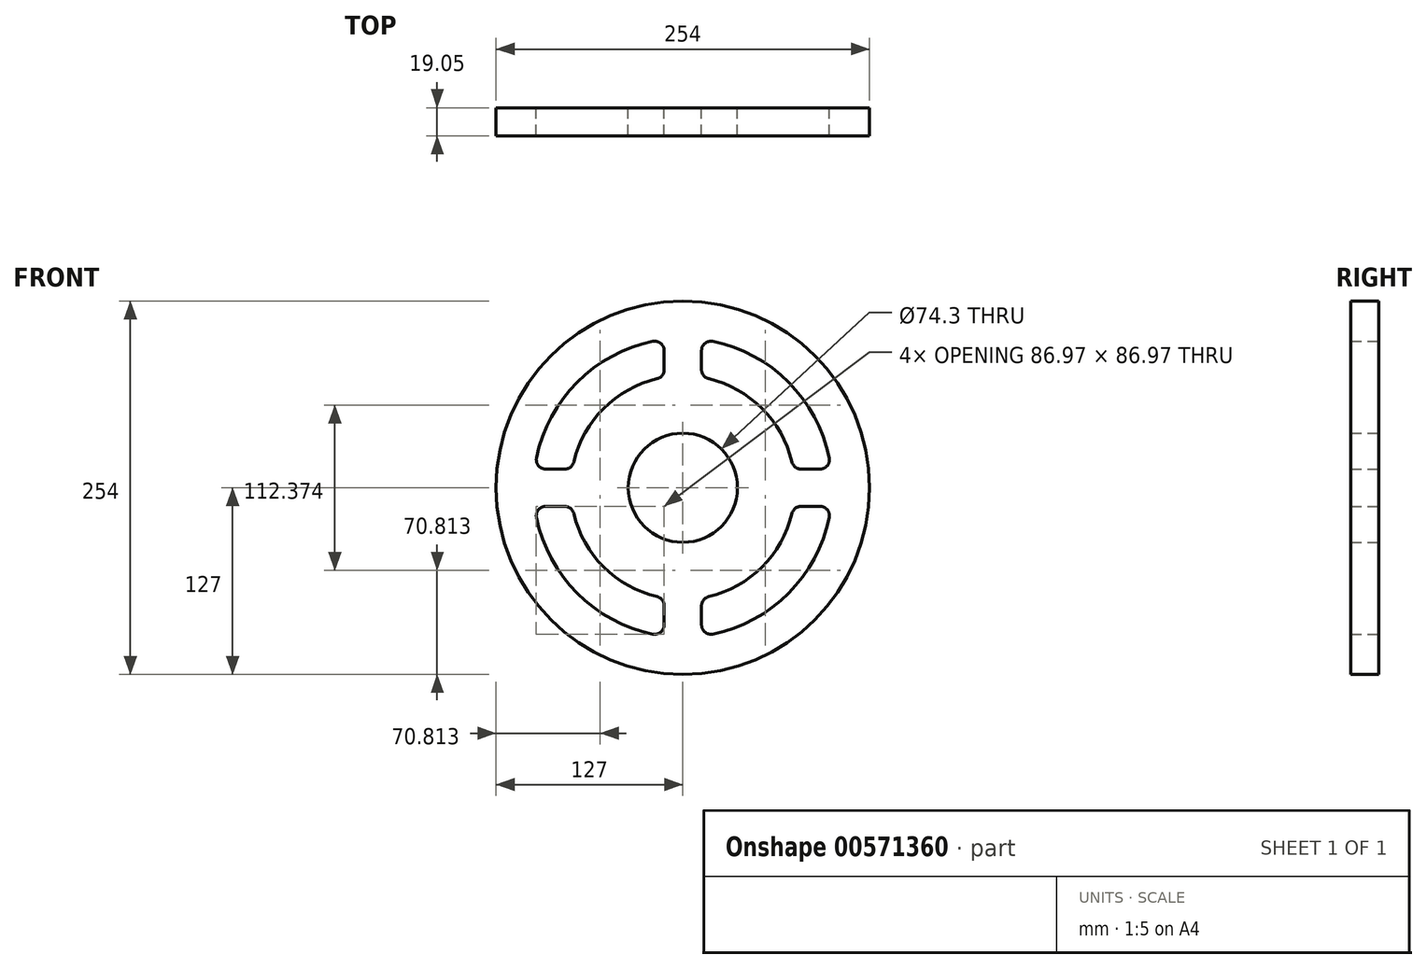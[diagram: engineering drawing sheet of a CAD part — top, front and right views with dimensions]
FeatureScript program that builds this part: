
annotation { "Feature Type Name" : "Feature", "Feature Type Description" : "" }
export const myFeature = defineFeature(function(context is Context, id is Id, definition is map)
    precondition{}
    {
        {
            var Q0;
            Q0=qCreatedBy(makeId("Front.planeOp"),FACE);
            var sketch = newSketch(context, id + "F0", { "sketchPlane" : qUnion([Q0])});
            skCircle(sketch, "E0", {"center": v(0, 0) * mm, "radius": 127 * mm});
            skCircle(sketch, "E1", {"center": v(0, 0) * mm, "radius": 32.39 * mm});
            skCircle(sketch, "E2", {"center": v(0, 0) * mm, "radius": 37.15 * mm});
            skSolve(sketch);
        }
        {
            var Q0;
            Q0=makeQuery(id+"F0.imprint","IMPRINT",FACE,{"disambiguationData":[TD([[makeQuery(id+"F0.imprint","IMPRINT",EDGE,{"derivedFrom":sQuery(id+"F0.wireOp",EDGE,"E0")}),1.0]])]});
            extrude(context, id + "F1", {"entities" : qUnion([Q0]), "depth" : 19.05 * mm, "offsetDistance" : 25.4 * mm});
        }
        {
            var Q0;
            Q0=makeQuery(id+"F1.opExtrude","CAP_FACE",FACE,{"disambiguationData":[OSD([sQuery(id+"F0.wireOp",EDGE,"E0"),sQuery(id+"F0.wireOp",EDGE,"E1")])],"isStart":true});
            var sketch = newSketch(context, id + "F2", { "sketchPlane" : qUnion([Q0])});
            skArc(sketch, "E3", {"start": v(74.14, 17.58) * mm, "mid": v(53.88, 53.88) * mm, "end": v(17.58, 74.14) * mm});
            skArc(sketch, "E4", {"start": v(99.55, 20.32) * mm, "mid": v(71.84, 71.84) * mm, "end": v(20.32, 99.55) * mm});
            skLineSegment(sketch, "E5.trimOffspring", {"start": v(-12.7, 80.32) * mm, "end": v(-12.7, 93.33) * mm});
            skLineSegment(sketch, "E6.trimOffspring", {"start": v(12.7, 80.32) * mm, "end": v(12.7, 93.33) * mm});
            skLineSegment(sketch, "E7.trimOffspring", {"start": v(80.32, 12.7) * mm, "end": v(93.33, 12.7) * mm});
            skLineSegment(sketch, "E8.trimOffspring", {"start": v(80.32, -12.7) * mm, "end": v(93.33, -12.7) * mm});
            skArc(sketch, "E9.trimOffspring", {"start": v(-17.58, 74.14) * mm, "mid": v(-53.88, 53.88) * mm, "end": v(-74.14, 17.58) * mm});
            skArc(sketch, "E10.trimOffspring", {"start": v(-20.32, 99.55) * mm, "mid": v(-71.84, 71.84) * mm, "end": v(-99.55, 20.32) * mm});
            skLineSegment(sketch, "E11.trimOffspring", {"start": v(-80.32, 12.7) * mm, "end": v(-93.33, 12.7) * mm});
            skLineSegment(sketch, "E12.trimOffspring", {"start": v(-80.32, -12.7) * mm, "end": v(-93.33, -12.7) * mm});
            skArc(sketch, "E13.trimOffspring", {"start": v(-74.14, -17.58) * mm, "mid": v(-53.88, -53.88) * mm, "end": v(-17.58, -74.14) * mm});
            skArc(sketch, "E14.trimOffspring", {"start": v(-99.55, -20.32) * mm, "mid": v(-71.84, -71.84) * mm, "end": v(-20.32, -99.55) * mm});
            skLineSegment(sketch, "E15.trimOffspring", {"start": v(-12.7, -80.32) * mm, "end": v(-12.7, -93.33) * mm});
            skLineSegment(sketch, "E16.trimOffspring", {"start": v(12.7, -80.32) * mm, "end": v(12.7, -93.33) * mm});
            skPoint(sketch, "E17.start.orphan", {"position": v(0, 12.7) * mm});
            skPoint(sketch, "E18.start.orphan", {"position": v(12.7, 0) * mm});
            skPoint(sketch, "E19.end.orphan", {"position": v(-12.7, 0) * mm});
            skPoint(sketch, "E20.start.orphan", {"position": v(0, -12.7) * mm});
            skArc(sketch, "E21.trimOffspring", {"start": v(20.32, -99.55) * mm, "mid": v(71.84, -71.84) * mm, "end": v(99.55, -20.32) * mm});
            skArc(sketch, "E22.trimOffspring", {"start": v(17.58, -74.14) * mm, "mid": v(53.88, -53.88) * mm, "end": v(74.14, -17.58) * mm});
            skPoint(sketch, "E23.visualSharp", {"position": v(-12.7, 100.8) * mm});
            skArc(sketch, "E23.filletArc", {"start": v(-12.7, 93.33) * mm, "mid": v(-15.03, 98.24) * mm, "end": v(-20.32, 99.55) * mm});
            skPoint(sketch, "E24.visualSharp", {"position": v(-12.7, 75.13) * mm});
            skArc(sketch, "E24.filletArc", {"start": v(-17.58, 74.14) * mm, "mid": v(-14.07, 76.38) * mm, "end": v(-12.7, 80.32) * mm});
            skPoint(sketch, "E25.visualSharp", {"position": v(-100.8, 12.7) * mm});
            skArc(sketch, "E25.filletArc", {"start": v(-99.55, 20.32) * mm, "mid": v(-98.24, 15.03) * mm, "end": v(-93.33, 12.7) * mm});
            skPoint(sketch, "E26.visualSharp", {"position": v(-75.13, 12.7) * mm});
            skArc(sketch, "E26.filletArc", {"start": v(-80.32, 12.7) * mm, "mid": v(-76.38, 14.07) * mm, "end": v(-74.14, 17.58) * mm});
            skPoint(sketch, "E27.visualSharp", {"position": v(-75.13, -12.7) * mm});
            skArc(sketch, "E27.filletArc", {"start": v(-74.14, -17.58) * mm, "mid": v(-76.38, -14.07) * mm, "end": v(-80.32, -12.7) * mm});
            skPoint(sketch, "E28.visualSharp", {"position": v(-100.8, -12.7) * mm});
            skArc(sketch, "E28.filletArc", {"start": v(-93.33, -12.7) * mm, "mid": v(-98.24, -15.03) * mm, "end": v(-99.55, -20.32) * mm});
            skPoint(sketch, "E29.visualSharp", {"position": v(-12.7, -100.8) * mm});
            skArc(sketch, "E29.filletArc", {"start": v(-20.32, -99.55) * mm, "mid": v(-15.03, -98.24) * mm, "end": v(-12.7, -93.33) * mm});
            skPoint(sketch, "E30.visualSharp", {"position": v(-12.7, -75.13) * mm});
            skArc(sketch, "E30.filletArc", {"start": v(-12.7, -80.32) * mm, "mid": v(-14.07, -76.38) * mm, "end": v(-17.58, -74.14) * mm});
            skPoint(sketch, "E31.visualSharp", {"position": v(12.7, -75.13) * mm});
            skArc(sketch, "E31.filletArc", {"start": v(17.58, -74.14) * mm, "mid": v(14.07, -76.38) * mm, "end": v(12.7, -80.32) * mm});
            skPoint(sketch, "E32.visualSharp", {"position": v(12.7, -100.8) * mm});
            skArc(sketch, "E32.filletArc", {"start": v(12.7, -93.33) * mm, "mid": v(15.03, -98.24) * mm, "end": v(20.32, -99.55) * mm});
            skPoint(sketch, "E33.visualSharp", {"position": v(100.8, -12.7) * mm});
            skArc(sketch, "E33.filletArc", {"start": v(99.55, -20.32) * mm, "mid": v(98.24, -15.03) * mm, "end": v(93.33, -12.7) * mm});
            skPoint(sketch, "E34.visualSharp", {"position": v(75.13, -12.7) * mm});
            skArc(sketch, "E34.filletArc", {"start": v(80.32, -12.7) * mm, "mid": v(76.38, -14.07) * mm, "end": v(74.14, -17.58) * mm});
            skPoint(sketch, "E35.visualSharp", {"position": v(75.13, 12.7) * mm});
            skArc(sketch, "E35.filletArc", {"start": v(74.14, 17.58) * mm, "mid": v(76.38, 14.07) * mm, "end": v(80.32, 12.7) * mm});
            skPoint(sketch, "E36.visualSharp", {"position": v(100.8, 12.7) * mm});
            skArc(sketch, "E36.filletArc", {"start": v(93.33, 12.7) * mm, "mid": v(98.24, 15.03) * mm, "end": v(99.55, 20.32) * mm});
            skPoint(sketch, "E37.visualSharp", {"position": v(12.7, 75.13) * mm});
            skArc(sketch, "E37.filletArc", {"start": v(12.7, 80.32) * mm, "mid": v(14.07, 76.38) * mm, "end": v(17.58, 74.14) * mm});
            skPoint(sketch, "E38.visualSharp", {"position": v(12.7, 100.8) * mm});
            skArc(sketch, "E38.filletArc", {"start": v(20.32, 99.55) * mm, "mid": v(15.03, 98.24) * mm, "end": v(12.7, 93.33) * mm});
            skSolve(sketch);
        }
        {
            var Q0;
            Q0=makeQuery(id+"F2.imprint","IMPRINT",FACE,{"disambiguationData":[TD([[makeQuery(id+"F2.imprint","IMPRINT",EDGE,{"derivedFrom":sQuery(id+"F2.wireOp",EDGE,"E5.trimOffspring")}),1.0]])]});
            var Q1;
            Q1=makeQuery(id+"F2.imprint","IMPRINT",FACE,{"disambiguationData":[TD([[makeQuery(id+"F2.imprint","IMPRINT",EDGE,{"derivedFrom":sQuery(id+"F2.wireOp",EDGE,"E3")}),-1.0]])]});
            var Q2;
            Q2=makeQuery(id+"F2.imprint","IMPRINT",FACE,{"disambiguationData":[TD([[makeQuery(id+"F2.imprint","IMPRINT",EDGE,{"derivedFrom":sQuery(id+"F2.wireOp",EDGE,"E8.trimOffspring")}),-1.0]])]});
            var Q3;
            Q3=makeQuery(id+"F2.imprint","IMPRINT",FACE,{"disambiguationData":[TD([[makeQuery(id+"F2.imprint","IMPRINT",EDGE,{"derivedFrom":sQuery(id+"F2.wireOp",EDGE,"E12.trimOffspring")}),1.0]])]});
            extrude(context, id + "F3", {"entities" : qUnion([Q0, Q1, Q2, Q3]), "operationType" : NewBodyOperationType.REMOVE, "oppositeDirection" : true, "depth" : 25.4 * mm, "offsetDistance" : 25.4 * mm});
        }
    });
